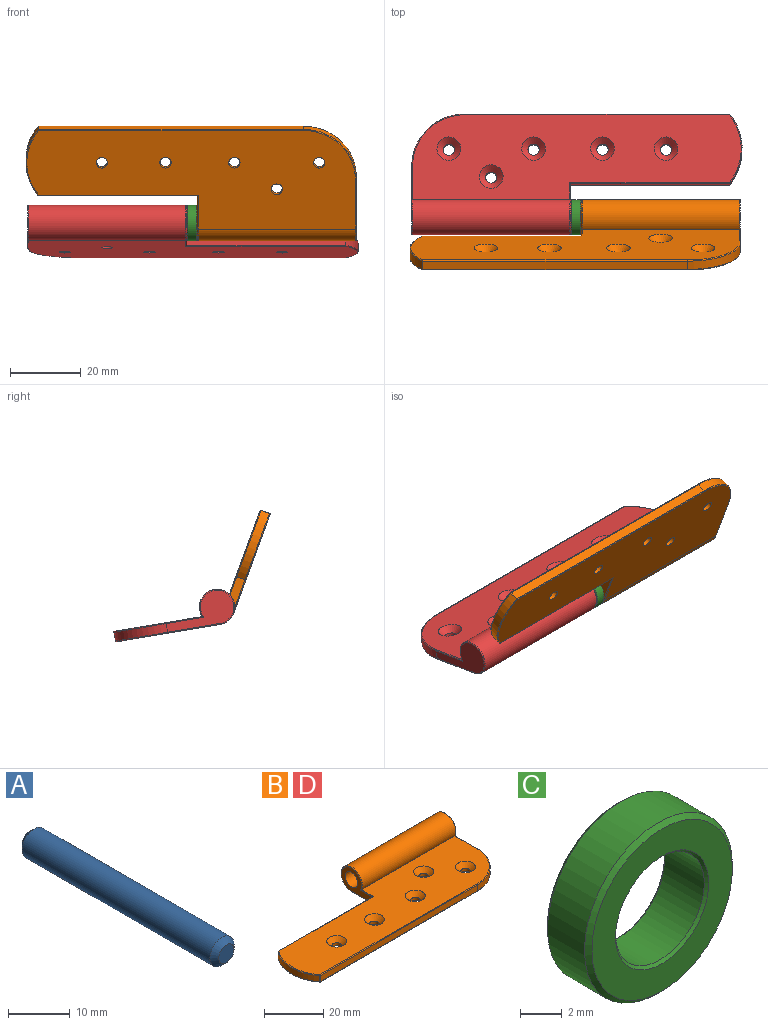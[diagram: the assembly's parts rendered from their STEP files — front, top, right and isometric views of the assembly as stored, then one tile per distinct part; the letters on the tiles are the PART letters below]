
ASSEMBLY  parts=4 mates=3
PART A: 5 faces, bbox 5.5x45x5.5 mm
  f0: cylinder r=2.75mm len=43mm, axis (0,-1,0), area 743mm2, adj f3,f4
  f1: plane 3.5x3.5mm, normal (0,1,0), area 9.6mm2, adj f3
  f2: plane 3.5x3.5mm, normal (0,-1,0), area 9.6mm2, adj f4
  f3: cone r=2.75mm half-angle=45deg, axis (0,-1,0), area 20mm2, adj f0,f1
  f4: cone r=1.75mm half-angle=45deg, axis (0,1,0), area 20mm2, adj f0,f2
PART B: 39 faces, bbox 96.1x36.7x10.9 mm
  f0: plane 14.75x9.5mm, normal (-1,0,0), area 60.2mm2, adj f1,f20,f25,f35,f38
  f1: plane 45x2.5mm, normal (0,1,0), area 112.5mm2, adj f0,f2,f22,f27
  f2: plane 2.86x0.13mm, normal (1,0,0), area 0.1mm2, adj f1,f3,f22,f24,f27,f29
  f3: cylinder r=16.02mm len=19.94mm, axis (0,0,-1), area 53.8mm2, adj f2,f24,f28,f29
  f4: plane 74.88x2.5mm, normal (0,-1,0), area 187.2mm2, adj f5,f23,f28,f31
  f5: cylinder r=15mm len=15mm, axis (0,0,-1), area 58.9mm2, adj f4,f6,f21,f32
  f6: plane 19.75x9.5mm, normal (1,0,0), area 100.9mm2, adj f5,f19,f33,f37
  f7: plane 93.02x25.17mm, normal (0,0,1), area 1821.1mm2, adj f10,f12,f14,f16,f18,f25,f27,f29
  f8: plane 93.02x29.75mm, normal (0,0,-1), area 2162.2mm2, adj f9,f11,f13,f15,f17,f19,f20,f21
  f9: cylinder r=1.6mm len=3.2mm, axis (0,0,1), area 12.5mm2, adj f8,f10
  f10: cone r=3.36mm half-angle=45deg, axis (0,0,1), area 38.8mm2, adj f7,f9
  f11: cylinder r=1.6mm len=3.2mm, axis (0,0,1), area 12.5mm2, adj f8,f12
  f12: cone r=3.36mm half-angle=45deg, axis (0,0,1), area 38.8mm2, adj f7,f11
  f13: cylinder r=1.6mm len=3.2mm, axis (0,0,1), area 12.5mm2, adj f8,f14
  f14: cone r=3.36mm half-angle=45deg, axis (0,0,1), area 38.8mm2, adj f7,f13
  f15: cylinder r=1.6mm len=3.2mm, axis (0,0,1), area 12.5mm2, adj f8,f16
  f16: cone r=3.36mm half-angle=45deg, axis (0,0,1), area 38.8mm2, adj f7,f15
  f17: cylinder r=1.6mm len=3.2mm, axis (0,0,1), area 12.5mm2, adj f8,f18
  f18: cone r=3.36mm half-angle=45deg, axis (0,0,1), area 38.8mm2, adj f7,f17
  f19: cylinder r=0.25mm len=15mm, axis (0,-1,0), area 5.9mm2, adj f6,f8,f21,f37
  f20: cylinder r=0.25mm len=10.25mm, axis (0,1,0), area 4mm2, adj f0,f8,f22,f38
  f21: torus R=14.75mm, axis (0,0,-1), area 9.2mm2, adj f5,f8,f19,f23
  f22: cylinder r=0.25mm len=45.25mm, axis (1,0,0), area 17.7mm2, adj f1,f2,f8,f20,f24
  f23: cylinder r=0.25mm len=74.88mm, axis (-1,0,0), area 29.4mm2, adj f4,f8,f21,f26
  f24: torus R=15.77mm, axis (0,0,-1), area 8.4mm2, adj f2,f3,f8,f22,f26
  f25: cylinder r=0.25mm len=6.07mm, axis (0,-1,0), area 2.2mm2, adj f0,f7,f27,f38
  f26: sphere r=0.25mm, area 0.1mm2, adj f23,f24,f28
  f27: cylinder r=0.25mm len=45.25mm, axis (-1,0,0), area 17.7mm2, adj f1,f2,f7,f25,f29
  f28: cylinder r=0.25mm len=2.5mm, axis (0,0,-1), area 0.6mm2, adj f3,f4,f26,f30
  f29: torus R=15.77mm, axis (0,0,-1), area 8.4mm2, adj f2,f3,f7,f27,f30
  f30: sphere r=0.25mm, area 0.1mm2, adj f28,f29,f31
  f31: cylinder r=0.25mm len=74.88mm, axis (1,0,0), area 29.4mm2, adj f4,f7,f30,f32
  f32: torus R=14.75mm, axis (0,0,-1), area 9.2mm2, adj f5,f7,f31,f33
  f33: cylinder r=0.25mm len=10.82mm, axis (0,1,0), area 4.1mm2, adj f6,f7,f32,f37
  f34: cylinder r=5mm len=44.5mm, axis (1,0,0), area 1140.1mm2, adj f7,f8,f37,f38
  f35: cylinder r=3mm len=22.5mm, axis (-1,0,0), area 424.1mm2, adj f0,f36
  f36: plane 6x6mm, normal (-1,0,0), area 28.3mm2, adj f35
  f37: torus R=4.75mm, axis (-1,0,0), area 9.9mm2, adj f6,f19,f33,f34
  f38: torus R=4.75mm, axis (1,0,0), area 9.9mm2, adj f0,f20,f25,f34
PART C: 8 faces, bbox 10x3x10 mm
  f0: cylinder r=5mm len=10mm, axis (0,1,0), area 78.5mm2, adj f3,f4
  f1: plane 9.5x9.5mm, normal (0,-1,0), area 39.7mm2, adj f4,f7
  f2: plane 9.5x9.5mm, normal (0,1,0), area 39.7mm2, adj f3,f6
  f3: cone r=5mm half-angle=45deg, axis (0,-1,0), area 10.8mm2, adj f0,f2
  f4: cone r=4.75mm half-angle=45deg, axis (0,1,0), area 10.8mm2, adj f0,f1
  f5: cylinder r=3mm len=6mm, axis (0,-1,0), area 50.9mm2, adj f6,f7
  f6: cone r=3.15mm half-angle=45deg, axis (0,1,0), area 4.1mm2, adj f2,f5
  f7: cone r=3mm half-angle=45deg, axis (0,-1,0), area 4.1mm2, adj f1,f5
PART D: same geometry as B
PLACE A rot(axis=(0,0,-1),90deg) t=(-45,-5,0)mm fixed
PLACE B rot(axis=(-1,0,0),69.8deg) t=(1.5,14.93,31.42)mm
PLACE C rot(axis=(0,0,-1),90deg) t=(-43.5,0,0)mm
PLACE D rot(axis=(0,0.08,1),180deg) t=(-91.5,58.76,-4.91)mm
MATE revolute D.f35 <-> A.f0  axis (1,0,0) through (-46.5,30,5)mm
MATE revolute B.f35 <-> A.f0  axis (-1,0,0) through (-43.5,30,5)mm
MATE fastened C.f0 <-> A.f0  axis (-1,0,0) through (-45,30,5)mm
